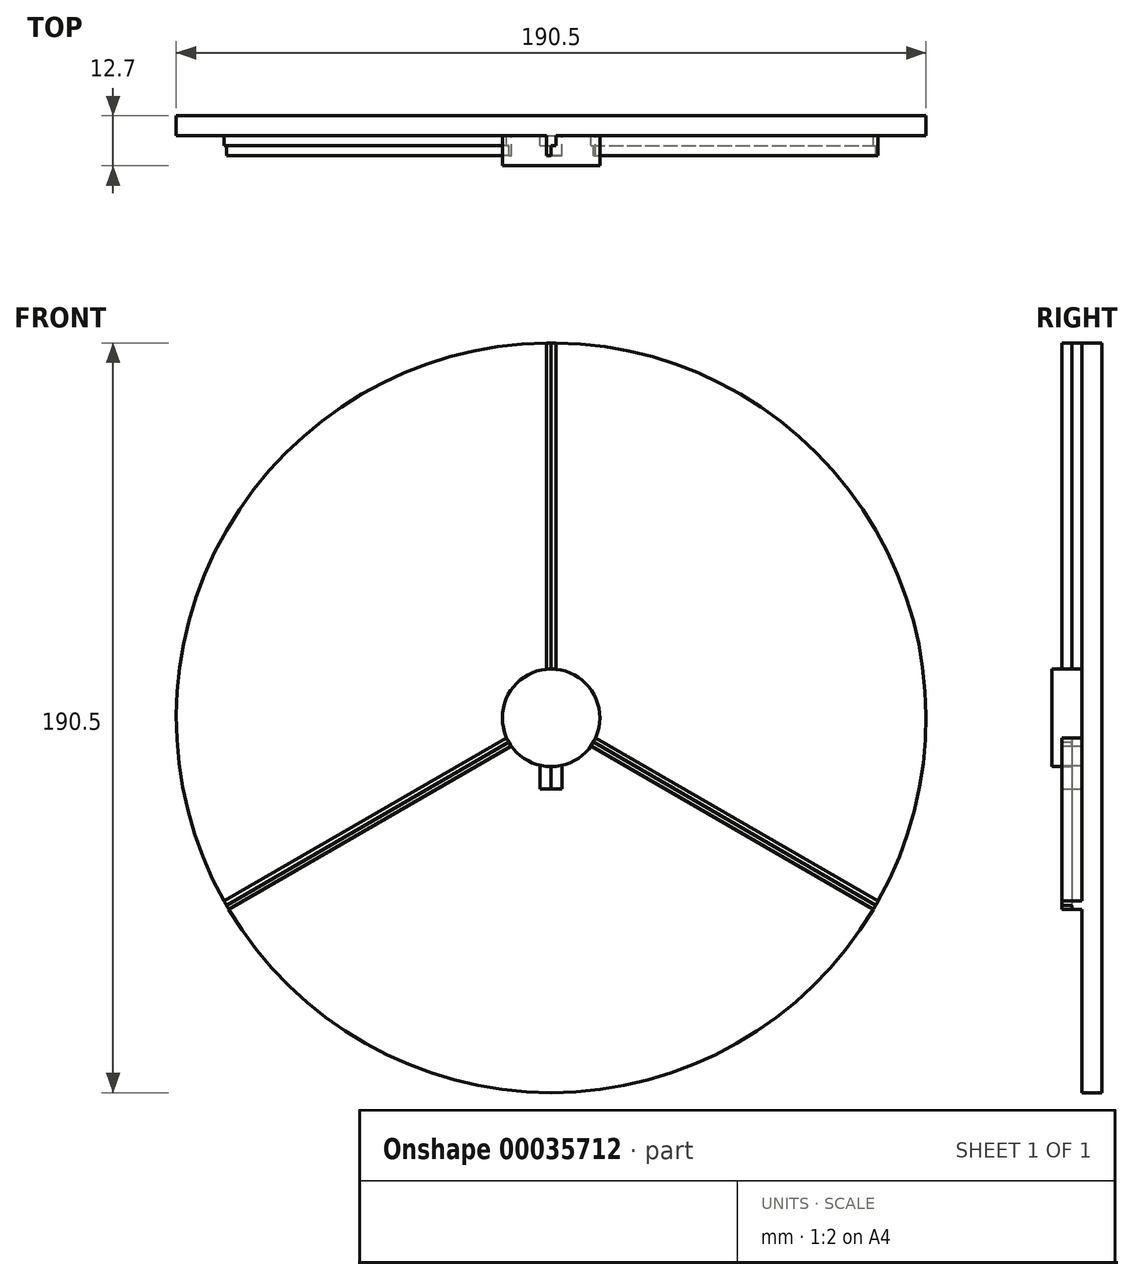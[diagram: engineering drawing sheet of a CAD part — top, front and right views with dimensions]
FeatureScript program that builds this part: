
annotation { "Feature Type Name" : "Feature", "Feature Type Description" : "" }
export const myFeature = defineFeature(function(context is Context, id is Id, definition is map)
    precondition{}
    {
        {
            var Q0;
            Q0=qCreatedBy(makeId("Front.planeOp"),FACE);
            var sketch = newSketch(context, id + "F0", { "sketchPlane" : qUnion([Q0])});
            skCircle(sketch, "E0", {"center": v(0, 0) * mm, "radius": 95.25 * mm});
            skCircle(sketch, "E1", {"center": v(0, 0) * mm, "radius": 12.4 * mm});
            skLineSegment(sketch, "E2", {"start": v(0, 0) * mm, "end": v(0, 95.25) * mm});
            skLineSegment(sketch, "E3", {"start": v(0, 0) * mm, "end": v(82.49, -47.62) * mm});
            skLineSegment(sketch, "E4", {"start": v(0, 0) * mm, "end": v(-1.2, 0) * mm, "construction": true});
            skLineSegment(sketch, "E5", {"start": v(-1.2, 0) * mm, "end": v(-1.2, 95.24) * mm});
            skCircle(sketch, "E6", {"center": v(0, 0) * mm, "radius": 1.2 * mm, "construction": true});
            skLineSegment(sketch, "E7.MirrorCS", {"start": v(0, 0) * mm, "end": v(1.2, 0) * mm, "construction": true});
            skLineSegment(sketch, "E8.MirrorCS", {"start": v(1.2, 0) * mm, "end": v(1.2, 95.24) * mm});
            skLineSegment(sketch, "E9", {"start": v(0, 0) * mm, "end": v(0.6, 1.03) * mm, "construction": true});
            skLineSegment(sketch, "E10", {"start": v(0.6, 1.03) * mm, "end": v(83.08, -46.6) * mm});
            skLineSegment(sketch, "E11.MirrorCS", {"start": v(-0.6, -1.03) * mm, "end": v(81.89, -48.65) * mm});
            skLineSegment(sketch, "E12.MirrorCS", {"start": v(0, 0) * mm, "end": v(-0.6, -1.03) * mm, "construction": true});
            skLineSegment(sketch, "E13.MirrorCS", {"start": v(0.6, -1.03) * mm, "end": v(-81.89, -48.65) * mm});
            skLineSegment(sketch, "E14.MirrorCS", {"start": v(0, 0) * mm, "end": v(-82.49, -47.62) * mm});
            skLineSegment(sketch, "E15.MirrorCS", {"start": v(-0.6, 1.03) * mm, "end": v(-83.08, -46.6) * mm});
            skLineSegment(sketch, "E16.MirrorCS", {"start": v(0, 0) * mm, "end": v(0.6, -1.03) * mm, "construction": true});
            skLineSegment(sketch, "E17.MirrorCS", {"start": v(0, 0) * mm, "end": v(-0.6, 1.03) * mm, "construction": true});
            skLineSegment(sketch, "E18", {"start": v(0, 0) * mm, "end": v(0, -95.25) * mm});
            skCircle(sketch, "E19", {"center": v(0, -14.57) * mm, "radius": 2.17 * mm});
            skCircle(sketch, "E20", {"center": v(0, -15.21) * mm, "radius": 2.82 * mm});
            skLineSegment(sketch, "E21", {"start": v(0, 0) * mm, "end": v(-2.82, 0) * mm, "construction": true});
            skLineSegment(sketch, "E22", {"start": v(-2.82, 0) * mm, "end": v(-2.82, -15.21) * mm});
            skLineSegment(sketch, "E23", {"start": v(0, 0) * mm, "end": v(-2.17, 0) * mm, "construction": true});
            skLineSegment(sketch, "E24", {"start": v(-2.17, 0) * mm, "end": v(-2.17, -14.57) * mm});
            skLineSegment(sketch, "E25", {"start": v(-2.82, -15.21) * mm, "end": v(-2.82, -18.03) * mm});
            skLineSegment(sketch, "E26", {"start": v(-2.82, -18.03) * mm, "end": v(0, -18.03) * mm});
            skLineSegment(sketch, "E27", {"start": v(-2.17, -14.57) * mm, "end": v(-2.17, -16.74) * mm});
            skLineSegment(sketch, "E28", {"start": v(-2.17, -16.74) * mm, "end": v(0, -16.74) * mm});
            skLineSegment(sketch, "E29.MirrorCS", {"start": v(2.17, -16.74) * mm, "end": v(0, -16.74) * mm});
            skLineSegment(sketch, "E30.MirrorCS", {"start": v(2.17, -14.57) * mm, "end": v(2.17, -16.74) * mm});
            skLineSegment(sketch, "E31.MirrorCS", {"start": v(2.82, -15.21) * mm, "end": v(2.82, -18.03) * mm});
            skLineSegment(sketch, "E32.MirrorCS", {"start": v(2.82, -18.03) * mm, "end": v(0, -18.03) * mm});
            skLineSegment(sketch, "E33.MirrorCS", {"start": v(2.82, 0) * mm, "end": v(2.82, -15.21) * mm});
            skLineSegment(sketch, "E34.MirrorCS", {"start": v(2.17, 0) * mm, "end": v(2.17, -14.57) * mm});
            skLineSegment(sketch, "E35.MirrorCS", {"start": v(0, 0) * mm, "end": v(2.17, 0) * mm, "construction": true});
            skLineSegment(sketch, "E36.MirrorCS", {"start": v(0, 0) * mm, "end": v(2.82, 0) * mm, "construction": true});
            skLineSegment(sketch, "E37", {"start": v(0, 0) * mm, "end": v(-82.49, 47.62) * mm});
            skLineSegment(sketch, "E38", {"start": v(0, 0) * mm, "end": v(82.49, 47.62) * mm});
            skLineSegment(sketch, "E39", {"start": v(0, 95.25) * mm, "end": v(0, 97.8) * mm});
            skLineSegment(sketch, "E40", {"start": v(0, 97.8) * mm, "end": v(-97.8, 97.8) * mm});
            skLineSegment(sketch, "E41", {"start": v(-97.8, 97.8) * mm, "end": v(-97.8, -97.8) * mm});
            skLineSegment(sketch, "E42", {"start": v(-97.8, -97.8) * mm, "end": v(0, -97.8) * mm});
            skLineSegment(sketch, "E43", {"start": v(0, -97.8) * mm, "end": v(0, -95.25) * mm});
            skLineSegment(sketch, "E44.MirrorCS", {"start": v(0, 97.8) * mm, "end": v(97.8, 97.8) * mm});
            skLineSegment(sketch, "E45.MirrorCS", {"start": v(97.8, 97.8) * mm, "end": v(97.8, -97.8) * mm});
            skLineSegment(sketch, "E46.MirrorCS", {"start": v(97.8, -97.8) * mm, "end": v(0, -97.8) * mm});
            skSolve(sketch);
        }
        {
            var Q0;
            {var subQ5=sQuery(id+"F0.wireOp",EDGE,"E39");Q0=makeQuery(id+"F0.imprint","IMPRINT",FACE,{"disambiguationData":[TD([[makeQuery(id+"F0.imprint","IMPRINT",EDGE,{"derivedFrom":subQ5}),-1.0]])]});}
            var Q1;
            {var subQ4=sQuery(id+"F0.wireOp",EDGE,"E39");Q1=makeQuery(id+"F0.imprint","IMPRINT",FACE,{"disambiguationData":[TD([[makeQuery(id+"F0.imprint","IMPRINT",EDGE,{"derivedFrom":subQ4}),1.0]])]});}
            var Q2;
            {var subQ3=sQuery(id+"F0.wireOp",EDGE,"E0");var subQ5=sQuery(id+"F0.wireOp",EDGE,"E5");var subQ7=makeQuery(id+"F0.imprint","INTERSECT",VERTEX,{"derivedFrom":[subQ3,subQ5]});Q2=makeQuery(id+"F0.imprint","IMPRINT",FACE,{"disambiguationData":[TD([[makeQuery(id+"F0.imprint","IMPRINT",EDGE,{"disambiguationData":[TD([[subQ7,-1.0]])],"derivedFrom":subQ3}),1.0]])]});}
            var Q3;
            {var subQ0=sQuery(id+"F0.wireOp",EDGE,"E24");var subQ3=sQuery(id+"F0.wireOp",EDGE,"E1");var subQ4=makeQuery(id+"F0.imprint","INTERSECT",VERTEX,{"derivedFrom":[subQ3,subQ0]});Q3=makeQuery(id+"F0.imprint","IMPRINT",FACE,{"disambiguationData":[TD([[makeQuery(id+"F0.imprint","IMPRINT",EDGE,{"disambiguationData":[TD([[subQ4,1.0]])],"derivedFrom":subQ0}),1.0]])]});}
            var Q4;
            {var subQ4=sQuery(id+"F0.wireOp",EDGE,"E31.MirrorCS");Q4=makeQuery(id+"F0.imprint","IMPRINT",FACE,{"disambiguationData":[TD([[makeQuery(id+"F0.imprint","IMPRINT",EDGE,{"derivedFrom":subQ4}),1.0]])]});}
            var Q5;
            {var subQ1=sQuery(id+"F0.wireOp",EDGE,"E8.MirrorCS");var subQ3=sQuery(id+"F0.wireOp",EDGE,"E1");var subQ5=makeQuery(id+"F0.imprint","INTERSECT",VERTEX,{"derivedFrom":[subQ3,subQ1]});Q5=makeQuery(id+"F0.imprint","IMPRINT",FACE,{"disambiguationData":[TD([[makeQuery(id+"F0.imprint","IMPRINT",EDGE,{"disambiguationData":[TD([[subQ5,1.0]])],"derivedFrom":subQ3}),1.0]])]});}
            var Q6;
            {var subQ1=sQuery(id+"F0.wireOp",EDGE,"E5");var subQ3=sQuery(id+"F0.wireOp",EDGE,"E1");var subQ5=makeQuery(id+"F0.imprint","INTERSECT",VERTEX,{"derivedFrom":[subQ3,subQ1]});Q6=makeQuery(id+"F0.imprint","IMPRINT",FACE,{"disambiguationData":[TD([[makeQuery(id+"F0.imprint","IMPRINT",EDGE,{"disambiguationData":[TD([[subQ5,-1.0]])],"derivedFrom":subQ3}),1.0]])]});}
            var Q7;
            {var subQ1=sQuery(id+"F0.wireOp",EDGE,"E13.MirrorCS");var subQ3=sQuery(id+"F0.wireOp",EDGE,"E1");var subQ5=makeQuery(id+"F0.imprint","INTERSECT",VERTEX,{"derivedFrom":[subQ3,subQ1]});Q7=makeQuery(id+"F0.imprint","IMPRINT",FACE,{"disambiguationData":[TD([[makeQuery(id+"F0.imprint","IMPRINT",EDGE,{"disambiguationData":[TD([[subQ5,-1.0]])],"derivedFrom":subQ3}),1.0]])]});}
            var Q8;
            {var subQ0=sQuery(id+"F0.wireOp",EDGE,"E33.MirrorCS");var subQ3=sQuery(id+"F0.wireOp",EDGE,"E1");var subQ4=makeQuery(id+"F0.imprint","INTERSECT",VERTEX,{"derivedFrom":[subQ3,subQ0]});Q8=makeQuery(id+"F0.imprint","IMPRINT",FACE,{"disambiguationData":[TD([[makeQuery(id+"F0.imprint","IMPRINT",EDGE,{"disambiguationData":[TD([[subQ4,-1.0]])],"derivedFrom":subQ3}),1.0]])]});}
            var Q9;
            {var subQ5=sQuery(id+"F0.wireOp",EDGE,"E25");Q9=makeQuery(id+"F0.imprint","IMPRINT",FACE,{"disambiguationData":[TD([[makeQuery(id+"F0.imprint","IMPRINT",EDGE,{"derivedFrom":subQ5}),-1.0]])]});}
            var Q10;
            {var subQ3=sQuery(id+"F0.wireOp",EDGE,"E0");var subQ5=sQuery(id+"F0.wireOp",EDGE,"E15.MirrorCS");var subQ7=makeQuery(id+"F0.imprint","INTERSECT",VERTEX,{"derivedFrom":[subQ3,subQ5]});Q10=makeQuery(id+"F0.imprint","IMPRINT",FACE,{"disambiguationData":[TD([[makeQuery(id+"F0.imprint","IMPRINT",EDGE,{"disambiguationData":[TD([[subQ7,1.0]])],"derivedFrom":subQ3}),1.0]])]});}
            var Q11;
            {var subQ0=sQuery(id+"F0.wireOp",EDGE,"E37");var subQ3=sQuery(id+"F0.wireOp",EDGE,"E1");var subQ4=makeQuery(id+"F0.imprint","INTERSECT",VERTEX,{"derivedFrom":[subQ3,subQ0]});Q11=makeQuery(id+"F0.imprint","IMPRINT",FACE,{"disambiguationData":[TD([[makeQuery(id+"F0.imprint","IMPRINT",EDGE,{"disambiguationData":[TD([[subQ4,-1.0]])],"derivedFrom":subQ3}),1.0]])]});}
            var Q12;
            {var subQ0=sQuery(id+"F0.wireOp",EDGE,"E10");var subQ3=sQuery(id+"F0.wireOp",EDGE,"E0");var subQ4=makeQuery(id+"F0.imprint","INTERSECT",VERTEX,{"derivedFrom":[subQ3,subQ0]});Q12=makeQuery(id+"F0.imprint","IMPRINT",FACE,{"disambiguationData":[TD([[makeQuery(id+"F0.imprint","IMPRINT",EDGE,{"disambiguationData":[TD([[subQ4,-1.0]])],"derivedFrom":subQ3}),1.0]])]});}
            var Q13;
            {var subQ3=sQuery(id+"F0.wireOp",EDGE,"E0");var subQ5=sQuery(id+"F0.wireOp",EDGE,"E8.MirrorCS");var subQ7=makeQuery(id+"F0.imprint","INTERSECT",VERTEX,{"derivedFrom":[subQ3,subQ5]});Q13=makeQuery(id+"F0.imprint","IMPRINT",FACE,{"disambiguationData":[TD([[makeQuery(id+"F0.imprint","IMPRINT",EDGE,{"disambiguationData":[TD([[subQ7,1.0]])],"derivedFrom":subQ3}),1.0]])]});}
            var Q14;
            {var subQ5=sQuery(id+"F0.wireOp",EDGE,"E1");var subQ7=sQuery(id+"F0.wireOp",EDGE,"E38");var subQ8=makeQuery(id+"F0.imprint","INTERSECT",VERTEX,{"derivedFrom":[subQ5,subQ7]});Q14=makeQuery(id+"F0.imprint","IMPRINT",FACE,{"disambiguationData":[TD([[makeQuery(id+"F0.imprint","IMPRINT",EDGE,{"disambiguationData":[TD([[subQ8,1.0]])],"derivedFrom":subQ5}),1.0]])]});}
            var Q15;
            {var subQ0=sQuery(id+"F0.wireOp",EDGE,"E34.MirrorCS");var subQ3=sQuery(id+"F0.wireOp",EDGE,"E1");var subQ4=makeQuery(id+"F0.imprint","INTERSECT",VERTEX,{"derivedFrom":[subQ3,subQ0]});Q15=makeQuery(id+"F0.imprint","IMPRINT",FACE,{"disambiguationData":[TD([[makeQuery(id+"F0.imprint","IMPRINT",EDGE,{"disambiguationData":[TD([[subQ4,1.0]])],"derivedFrom":subQ0}),-1.0]])]});}
            var Q16;
            {var subQ0=sQuery(id+"F0.wireOp",EDGE,"E24");var subQ3=sQuery(id+"F0.wireOp",EDGE,"E1");var subQ4=makeQuery(id+"F0.imprint","INTERSECT",VERTEX,{"derivedFrom":[subQ3,subQ0]});Q16=makeQuery(id+"F0.imprint","IMPRINT",FACE,{"disambiguationData":[TD([[makeQuery(id+"F0.imprint","IMPRINT",EDGE,{"disambiguationData":[TD([[subQ4,-1.0]])],"derivedFrom":subQ0}),1.0]])]});}
            var Q17;
            {var subQ3=sQuery(id+"F0.wireOp",EDGE,"E3");var subQ5=sQuery(id+"F0.wireOp",EDGE,"E1");var subQ7=makeQuery(id+"F0.imprint","INTERSECT",VERTEX,{"derivedFrom":[subQ5,subQ3]});Q17=makeQuery(id+"F0.imprint","IMPRINT",FACE,{"disambiguationData":[TD([[makeQuery(id+"F0.imprint","IMPRINT",EDGE,{"disambiguationData":[TD([[subQ7,-1.0]])],"derivedFrom":subQ5}),1.0]])]});}
            var Q18;
            {var subQ3=sQuery(id+"F0.wireOp",EDGE,"E1");var subQ5=sQuery(id+"F0.wireOp",EDGE,"E22");var subQ7=makeQuery(id+"F0.imprint","INTERSECT",VERTEX,{"derivedFrom":[subQ3,subQ5]});Q18=makeQuery(id+"F0.imprint","IMPRINT",FACE,{"disambiguationData":[TD([[makeQuery(id+"F0.imprint","IMPRINT",EDGE,{"disambiguationData":[TD([[subQ7,-1.0]])],"derivedFrom":subQ3}),1.0]])]});}
            var Q19;
            {var subQ1=sQuery(id+"F0.wireOp",EDGE,"E15.MirrorCS");var subQ5=sQuery(id+"F0.wireOp",EDGE,"E1");var subQ6=makeQuery(id+"F0.imprint","INTERSECT",VERTEX,{"derivedFrom":[subQ5,subQ1]});Q19=makeQuery(id+"F0.imprint","IMPRINT",FACE,{"disambiguationData":[TD([[makeQuery(id+"F0.imprint","IMPRINT",EDGE,{"disambiguationData":[TD([[subQ6,-1.0]])],"derivedFrom":subQ5}),1.0]])]});}
            var Q20;
            {var subQ0=sQuery(id+"F0.wireOp",EDGE,"E1");var subQ3=sQuery(id+"F0.wireOp",EDGE,"E8.MirrorCS");var subQ4=makeQuery(id+"F0.imprint","INTERSECT",VERTEX,{"derivedFrom":[subQ0,subQ3]});Q20=makeQuery(id+"F0.imprint","IMPRINT",FACE,{"disambiguationData":[TD([[makeQuery(id+"F0.imprint","IMPRINT",EDGE,{"disambiguationData":[TD([[subQ4,-1.0]])],"derivedFrom":subQ0}),1.0]])]});}
            var Q21;
            {var subQ0=sQuery(id+"F0.wireOp",EDGE,"E14.MirrorCS");var subQ3=sQuery(id+"F0.wireOp",EDGE,"E0");var subQ4=makeQuery(id+"F0.imprint","INTERSECT",VERTEX,{"derivedFrom":[subQ3,subQ0]});Q21=makeQuery(id+"F0.imprint","IMPRINT",FACE,{"disambiguationData":[TD([[makeQuery(id+"F0.imprint","IMPRINT",EDGE,{"disambiguationData":[TD([[subQ4,1.0]])],"derivedFrom":subQ3}),1.0]])]});}
            var Q22;
            {var subQ5=sQuery(id+"F0.wireOp",EDGE,"E1");var subQ7=sQuery(id+"F0.wireOp",EDGE,"E2");var subQ8=makeQuery(id+"F0.imprint","INTERSECT",VERTEX,{"derivedFrom":[subQ5,subQ7]});Q22=makeQuery(id+"F0.imprint","IMPRINT",FACE,{"disambiguationData":[TD([[makeQuery(id+"F0.imprint","IMPRINT",EDGE,{"disambiguationData":[TD([[subQ8,-1.0]])],"derivedFrom":subQ5}),1.0]])]});}
            var Q23;
            {var subQ3=sQuery(id+"F0.wireOp",EDGE,"E0");var subQ5=sQuery(id+"F0.wireOp",EDGE,"E13.MirrorCS");var subQ7=makeQuery(id+"F0.imprint","INTERSECT",VERTEX,{"derivedFrom":[subQ3,subQ5]});Q23=makeQuery(id+"F0.imprint","IMPRINT",FACE,{"disambiguationData":[TD([[makeQuery(id+"F0.imprint","IMPRINT",EDGE,{"disambiguationData":[TD([[subQ7,1.0]])],"derivedFrom":subQ3}),1.0]])]});}
            var Q24;
            {var subQ0=sQuery(id+"F0.wireOp",EDGE,"E24");var subQ3=sQuery(id+"F0.wireOp",EDGE,"E13.MirrorCS");var subQ4=makeQuery(id+"F0.imprint","INTERSECT",VERTEX,{"derivedFrom":[subQ3,subQ0]});Q24=makeQuery(id+"F0.imprint","IMPRINT",FACE,{"disambiguationData":[TD([[makeQuery(id+"F0.imprint","IMPRINT",EDGE,{"disambiguationData":[TD([[subQ4,-1.0]])],"derivedFrom":subQ3}),-1.0]])]});}
            var Q25;
            {var subQ0=sQuery(id+"F0.wireOp",EDGE,"E2");var subQ1=sQuery(id+"F0.wireOp",EDGE,"E1");var subQ2=makeQuery(id+"F0.imprint","INTERSECT",VERTEX,{"derivedFrom":[subQ1,subQ0]});Q25=makeQuery(id+"F0.imprint","IMPRINT",FACE,{"disambiguationData":[TD([[makeQuery(id+"F0.imprint","IMPRINT",EDGE,{"disambiguationData":[TD([[subQ2,-1.0]])],"derivedFrom":subQ1}),-1.0]])]});}
            var Q26;
            {var subQ1=sQuery(id+"F0.wireOp",EDGE,"E11.MirrorCS");var subQ5=sQuery(id+"F0.wireOp",EDGE,"E1");var subQ6=makeQuery(id+"F0.imprint","INTERSECT",VERTEX,{"derivedFrom":[subQ5,subQ1]});Q26=makeQuery(id+"F0.imprint","IMPRINT",FACE,{"disambiguationData":[TD([[makeQuery(id+"F0.imprint","IMPRINT",EDGE,{"disambiguationData":[TD([[subQ6,-1.0]])],"derivedFrom":subQ5}),1.0]])]});}
            var Q27;
            {var subQ1=sQuery(id+"F0.wireOp",EDGE,"E14.MirrorCS");var subQ5=sQuery(id+"F0.wireOp",EDGE,"E1");var subQ6=makeQuery(id+"F0.imprint","INTERSECT",VERTEX,{"derivedFrom":[subQ5,subQ1]});Q27=makeQuery(id+"F0.imprint","IMPRINT",FACE,{"disambiguationData":[TD([[makeQuery(id+"F0.imprint","IMPRINT",EDGE,{"disambiguationData":[TD([[subQ6,-1.0]])],"derivedFrom":subQ5}),1.0]])]});}
            var Q28;
            {var subQ3=sQuery(id+"F0.wireOp",EDGE,"E0");var subQ5=sQuery(id+"F0.wireOp",EDGE,"E3");var subQ7=makeQuery(id+"F0.imprint","INTERSECT",VERTEX,{"derivedFrom":[subQ3,subQ5]});Q28=makeQuery(id+"F0.imprint","IMPRINT",FACE,{"disambiguationData":[TD([[makeQuery(id+"F0.imprint","IMPRINT",EDGE,{"disambiguationData":[TD([[subQ7,-1.0]])],"derivedFrom":subQ3}),1.0]])]});}
            var Q29;
            {var subQ3=sQuery(id+"F0.wireOp",EDGE,"E0");var subQ5=sQuery(id+"F0.wireOp",EDGE,"E3");var subQ7=makeQuery(id+"F0.imprint","INTERSECT",VERTEX,{"derivedFrom":[subQ3,subQ5]});Q29=makeQuery(id+"F0.imprint","IMPRINT",FACE,{"disambiguationData":[TD([[makeQuery(id+"F0.imprint","IMPRINT",EDGE,{"disambiguationData":[TD([[subQ7,1.0]])],"derivedFrom":subQ3}),1.0]])]});}
            var Q30;
            {var subQ1=sQuery(id+"F0.wireOp",EDGE,"E1");var subQ5=sQuery(id+"F0.wireOp",EDGE,"E8.MirrorCS");var subQ6=makeQuery(id+"F0.imprint","INTERSECT",VERTEX,{"derivedFrom":[subQ1,subQ5]});Q30=makeQuery(id+"F0.imprint","IMPRINT",FACE,{"disambiguationData":[TD([[makeQuery(id+"F0.imprint","IMPRINT",EDGE,{"disambiguationData":[TD([[subQ6,-1.0]])],"derivedFrom":subQ1}),-1.0]])]});}
            var Q31;
            {var subQ3=sQuery(id+"F0.wireOp",EDGE,"E3");var subQ5=sQuery(id+"F0.wireOp",EDGE,"E6");var subQ6=makeQuery(id+"F0.imprint","INTERSECT",VERTEX,{"derivedFrom":[subQ3,subQ5]});Q31=makeQuery(id+"F0.imprint","IMPRINT",FACE,{"disambiguationData":[TD([[makeQuery(id+"F0.imprint","IMPRINT",EDGE,{"disambiguationData":[TD([[subQ6,-1.0]])],"derivedFrom":subQ3}),-1.0]])]});}
            var Q32;
            {var subQ0=sQuery(id+"F0.wireOp",EDGE,"E34.MirrorCS");var subQ3=sQuery(id+"F0.wireOp",EDGE,"E3");var subQ4=makeQuery(id+"F0.imprint","INTERSECT",VERTEX,{"derivedFrom":[subQ3,subQ0]});Q32=makeQuery(id+"F0.imprint","IMPRINT",FACE,{"disambiguationData":[TD([[makeQuery(id+"F0.imprint","IMPRINT",EDGE,{"disambiguationData":[TD([[subQ4,-1.0]])],"derivedFrom":subQ3}),-1.0]])]});}
            var Q33;
            {var subQ0=sQuery(id+"F0.wireOp",EDGE,"E19");var subQ1=makeQuery(id+"F0.imprint","INTERSECT",VERTEX,{"derivedFrom":[subQ0,sQuery(id+"F0.wireOp",EDGE,"E30.MirrorCS"),sQuery(id+"F0.wireOp",EDGE,"E34.MirrorCS")]});Q33=makeQuery(id+"F0.imprint","IMPRINT",FACE,{"disambiguationData":[TD([[makeQuery(id+"F0.imprint","IMPRINT",EDGE,{"disambiguationData":[TD([[subQ1,-1.0]])],"derivedFrom":subQ0}),1.0]])]});}
            var Q34;
            {var subQ0=sQuery(id+"F0.wireOp",EDGE,"E6");var subQ1=sQuery(id+"F0.wireOp",EDGE,"E14.MirrorCS");var subQ2=makeQuery(id+"F0.imprint","INTERSECT",VERTEX,{"derivedFrom":[subQ0,subQ1]});Q34=makeQuery(id+"F0.imprint","IMPRINT",FACE,{"disambiguationData":[TD([[makeQuery(id+"F0.imprint","IMPRINT",EDGE,{"disambiguationData":[TD([[subQ2,-1.0]])],"derivedFrom":subQ1}),1.0]])]});}
            var Q35;
            {var subQ3=sQuery(id+"F0.wireOp",EDGE,"E1");var subQ5=sQuery(id+"F0.wireOp",EDGE,"E34.MirrorCS");var subQ7=makeQuery(id+"F0.imprint","INTERSECT",VERTEX,{"derivedFrom":[subQ3,subQ5]});Q35=makeQuery(id+"F0.imprint","IMPRINT",FACE,{"disambiguationData":[TD([[makeQuery(id+"F0.imprint","IMPRINT",EDGE,{"disambiguationData":[TD([[subQ7,-1.0]])],"derivedFrom":subQ3}),1.0]])]});}
            var Q36;
            {var subQ3=sQuery(id+"F0.wireOp",EDGE,"E1");var subQ5=sQuery(id+"F0.wireOp",EDGE,"E22");var subQ6=makeQuery(id+"F0.imprint","INTERSECT",VERTEX,{"derivedFrom":[subQ3,subQ5]});Q36=makeQuery(id+"F0.imprint","IMPRINT",FACE,{"disambiguationData":[TD([[makeQuery(id+"F0.imprint","IMPRINT",EDGE,{"disambiguationData":[TD([[subQ6,-1.0]])],"derivedFrom":subQ3}),-1.0]])]});}
            var Q37;
            {var subQ1=sQuery(id+"F0.wireOp",EDGE,"E1");var subQ5=sQuery(id+"F0.wireOp",EDGE,"E34.MirrorCS");var subQ7=makeQuery(id+"F0.imprint","INTERSECT",VERTEX,{"derivedFrom":[subQ1,subQ5]});Q37=makeQuery(id+"F0.imprint","IMPRINT",FACE,{"disambiguationData":[TD([[makeQuery(id+"F0.imprint","IMPRINT",EDGE,{"disambiguationData":[TD([[subQ7,-1.0]])],"derivedFrom":subQ1}),-1.0]])]});}
            var Q38;
            {var subQ1=sQuery(id+"F0.wireOp",EDGE,"E27");Q38=makeQuery(id+"F0.imprint","IMPRINT",FACE,{"disambiguationData":[TD([[makeQuery(id+"F0.imprint","IMPRINT",EDGE,{"derivedFrom":subQ1}),1.0]])]});}
            var Q39;
            {var subQ0=sQuery(id+"F0.wireOp",EDGE,"E34.MirrorCS");var subQ1=sQuery(id+"F0.wireOp",EDGE,"E20");var subQ2=makeQuery(id+"F0.imprint","INTERSECT",VERTEX,{"derivedFrom":[subQ1,subQ0]});Q39=makeQuery(id+"F0.imprint","IMPRINT",FACE,{"disambiguationData":[TD([[makeQuery(id+"F0.imprint","IMPRINT",EDGE,{"disambiguationData":[TD([[subQ2,-1.0]])],"derivedFrom":subQ0}),-1.0]])]});}
            var Q40;
            {var subQ0=sQuery(id+"F0.wireOp",EDGE,"E34.MirrorCS");var subQ3=sQuery(id+"F0.wireOp",EDGE,"E1");var subQ4=makeQuery(id+"F0.imprint","INTERSECT",VERTEX,{"derivedFrom":[subQ3,subQ0]});Q40=makeQuery(id+"F0.imprint","IMPRINT",FACE,{"disambiguationData":[TD([[makeQuery(id+"F0.imprint","IMPRINT",EDGE,{"disambiguationData":[TD([[subQ4,-1.0]])],"derivedFrom":subQ0}),-1.0]])]});}
            var Q41;
            {var subQ1=sQuery(id+"F0.wireOp",EDGE,"E27");Q41=makeQuery(id+"F0.imprint","IMPRINT",FACE,{"disambiguationData":[TD([[makeQuery(id+"F0.imprint","IMPRINT",EDGE,{"derivedFrom":subQ1}),-1.0]])]});}
            var Q42;
            {var subQ0=sQuery(id+"F0.wireOp",EDGE,"E24");var subQ1=sQuery(id+"F0.wireOp",EDGE,"E20");var subQ2=makeQuery(id+"F0.imprint","INTERSECT",VERTEX,{"derivedFrom":[subQ1,subQ0]});Q42=makeQuery(id+"F0.imprint","IMPRINT",FACE,{"disambiguationData":[TD([[makeQuery(id+"F0.imprint","IMPRINT",EDGE,{"disambiguationData":[TD([[subQ2,-1.0]])],"derivedFrom":subQ0}),1.0]])]});}
            var Q43;
            {var subQ5=sQuery(id+"F0.wireOp",EDGE,"E29.MirrorCS");Q43=makeQuery(id+"F0.imprint","IMPRINT",FACE,{"disambiguationData":[TD([[makeQuery(id+"F0.imprint","IMPRINT",EDGE,{"derivedFrom":subQ5}),1.0]])]});}
            var Q44;
            {var subQ0=sQuery(id+"F0.wireOp",EDGE,"E19");var subQ3=makeQuery(id+"F0.imprint","INTERSECT",VERTEX,{"derivedFrom":[subQ0,sQuery(id+"F0.wireOp",EDGE,"E24"),sQuery(id+"F0.wireOp",EDGE,"E27")]});Q44=makeQuery(id+"F0.imprint","IMPRINT",FACE,{"disambiguationData":[TD([[makeQuery(id+"F0.imprint","IMPRINT",EDGE,{"disambiguationData":[TD([[subQ3,1.0]])],"derivedFrom":subQ0}),1.0]])]});}
            var Q45;
            {var subQ1=sQuery(id+"F0.wireOp",EDGE,"E29.MirrorCS");Q45=makeQuery(id+"F0.imprint","IMPRINT",FACE,{"disambiguationData":[TD([[makeQuery(id+"F0.imprint","IMPRINT",EDGE,{"derivedFrom":subQ1}),-1.0]])]});}
            var Q46;
            {var subQ1=sQuery(id+"F0.wireOp",EDGE,"E25");Q46=makeQuery(id+"F0.imprint","IMPRINT",FACE,{"disambiguationData":[TD([[makeQuery(id+"F0.imprint","IMPRINT",EDGE,{"derivedFrom":subQ1}),1.0]])]});}
            var Q47;
            {var subQ1=sQuery(id+"F0.wireOp",EDGE,"E31.MirrorCS");Q47=makeQuery(id+"F0.imprint","IMPRINT",FACE,{"disambiguationData":[TD([[makeQuery(id+"F0.imprint","IMPRINT",EDGE,{"derivedFrom":subQ1}),-1.0]])]});}
            var Q48;
            {var subQ1=sQuery(id+"F0.wireOp",EDGE,"E15.MirrorCS");var subQ3=sQuery(id+"F0.wireOp",EDGE,"E21");var subQ5=makeQuery(id+"F0.imprint","INTERSECT",VERTEX,{"derivedFrom":[subQ1,subQ3]});Q48=makeQuery(id+"F0.imprint","IMPRINT",FACE,{"disambiguationData":[TD([[makeQuery(id+"F0.imprint","IMPRINT",EDGE,{"disambiguationData":[TD([[subQ5,-1.0]])],"derivedFrom":subQ1}),-1.0]])]});}
            var Q49;
            {var subQ0=sQuery(id+"F0.wireOp",EDGE,"E3");var subQ3=sQuery(id+"F0.wireOp",EDGE,"E34.MirrorCS");var subQ4=makeQuery(id+"F0.imprint","INTERSECT",VERTEX,{"derivedFrom":[subQ0,subQ3]});Q49=makeQuery(id+"F0.imprint","IMPRINT",FACE,{"disambiguationData":[TD([[makeQuery(id+"F0.imprint","IMPRINT",EDGE,{"disambiguationData":[TD([[subQ4,-1.0]])],"derivedFrom":subQ0}),1.0]])]});}
            var Q50;
            {var subQ0=sQuery(id+"F0.wireOp",EDGE,"E24");var subQ1=sQuery(id+"F0.wireOp",EDGE,"E14.MirrorCS");var subQ2=makeQuery(id+"F0.imprint","INTERSECT",VERTEX,{"derivedFrom":[subQ1,subQ0]});Q50=makeQuery(id+"F0.imprint","IMPRINT",FACE,{"disambiguationData":[TD([[makeQuery(id+"F0.imprint","IMPRINT",EDGE,{"disambiguationData":[TD([[subQ2,-1.0]])],"derivedFrom":subQ1}),-1.0]])]});}
            var Q51;
            {var subQ1=sQuery(id+"F0.wireOp",EDGE,"E14.MirrorCS");var subQ5=sQuery(id+"F0.wireOp",EDGE,"E6");var subQ7=makeQuery(id+"F0.imprint","INTERSECT",VERTEX,{"derivedFrom":[subQ5,subQ1]});Q51=makeQuery(id+"F0.imprint","IMPRINT",FACE,{"disambiguationData":[TD([[makeQuery(id+"F0.imprint","IMPRINT",EDGE,{"disambiguationData":[TD([[subQ7,-1.0]])],"derivedFrom":subQ1}),-1.0]])]});}
            var Q52;
            {var subQ1=sQuery(id+"F0.wireOp",EDGE,"E3");var subQ5=sQuery(id+"F0.wireOp",EDGE,"E6");var subQ7=makeQuery(id+"F0.imprint","INTERSECT",VERTEX,{"derivedFrom":[subQ1,subQ5]});Q52=makeQuery(id+"F0.imprint","IMPRINT",FACE,{"disambiguationData":[TD([[makeQuery(id+"F0.imprint","IMPRINT",EDGE,{"disambiguationData":[TD([[subQ7,-1.0]])],"derivedFrom":subQ1}),1.0]])]});}
            var Q53;
            {var subQ0=sQuery(id+"F0.wireOp",EDGE,"E37");var subQ3=sQuery(id+"F0.wireOp",EDGE,"E6");var subQ4=makeQuery(id+"F0.imprint","INTERSECT",VERTEX,{"derivedFrom":[subQ3,subQ0]});Q53=makeQuery(id+"F0.imprint","IMPRINT",FACE,{"disambiguationData":[TD([[makeQuery(id+"F0.imprint","IMPRINT",EDGE,{"disambiguationData":[TD([[subQ4,1.0]])],"derivedFrom":subQ3}),-1.0]])]});}
            var Q54;
            {var subQ0=sQuery(id+"F0.wireOp",EDGE,"E16.MirrorCS");Q54=makeQuery(id+"F0.imprint","IMPRINT",FACE,{"disambiguationData":[TD([[makeQuery(id+"F0.imprint","IMPRINT",EDGE,{"derivedFrom":subQ0}),-1.0]])]});}
            var Q55;
            {var subQ3=sQuery(id+"F0.wireOp",EDGE,"E36.MirrorCS");var subQ5=makeQuery(id+"F0.imprint","INTERSECT",VERTEX,{"derivedFrom":[sQuery(id+"F0.wireOp",EDGE,"E34.MirrorCS"),subQ3]});Q55=makeQuery(id+"F0.imprint","IMPRINT",FACE,{"disambiguationData":[TD([[makeQuery(id+"F0.imprint","IMPRINT",EDGE,{"disambiguationData":[TD([[subQ5,-1.0]])],"derivedFrom":subQ3}),1.0]])]});}
            var Q56;
            {var subQ0=sQuery(id+"F0.wireOp",EDGE,"E18");var subQ3=sQuery(id+"F0.wireOp",EDGE,"E6");var subQ4=makeQuery(id+"F0.imprint","INTERSECT",VERTEX,{"derivedFrom":[subQ3,subQ0]});Q56=makeQuery(id+"F0.imprint","IMPRINT",FACE,{"disambiguationData":[TD([[makeQuery(id+"F0.imprint","IMPRINT",EDGE,{"disambiguationData":[TD([[subQ4,1.0]])],"derivedFrom":subQ3}),-1.0]])]});}
            var Q57;
            {var subQ1=sQuery(id+"F0.wireOp",EDGE,"E18");var subQ3=sQuery(id+"F0.wireOp",EDGE,"E6");var subQ5=makeQuery(id+"F0.imprint","INTERSECT",VERTEX,{"derivedFrom":[subQ3,subQ1]});Q57=makeQuery(id+"F0.imprint","IMPRINT",FACE,{"disambiguationData":[TD([[makeQuery(id+"F0.imprint","IMPRINT",EDGE,{"disambiguationData":[TD([[subQ5,-1.0]])],"derivedFrom":subQ3}),-1.0]])]});}
            var Q58;
            {var subQ0=sQuery(id+"F0.wireOp",EDGE,"E37");var subQ3=sQuery(id+"F0.wireOp",EDGE,"E6");var subQ4=makeQuery(id+"F0.imprint","INTERSECT",VERTEX,{"derivedFrom":[subQ3,subQ0]});Q58=makeQuery(id+"F0.imprint","IMPRINT",FACE,{"disambiguationData":[TD([[makeQuery(id+"F0.imprint","IMPRINT",EDGE,{"disambiguationData":[TD([[subQ4,-1.0]])],"derivedFrom":subQ3}),-1.0]])]});}
            var Q59;
            {var subQ1=sQuery(id+"F0.wireOp",EDGE,"E6");var subQ3=sQuery(id+"F0.wireOp",EDGE,"E3");var subQ5=makeQuery(id+"F0.imprint","INTERSECT",VERTEX,{"derivedFrom":[subQ3,subQ1]});Q59=makeQuery(id+"F0.imprint","IMPRINT",FACE,{"disambiguationData":[TD([[makeQuery(id+"F0.imprint","IMPRINT",EDGE,{"disambiguationData":[TD([[subQ5,-1.0]])],"derivedFrom":subQ1}),1.0]])]});}
            var Q60;
            {var subQ3=sQuery(id+"F0.wireOp",EDGE,"E17.MirrorCS");Q60=makeQuery(id+"F0.imprint","IMPRINT",FACE,{"disambiguationData":[TD([[makeQuery(id+"F0.imprint","IMPRINT",EDGE,{"derivedFrom":subQ3}),1.0]])]});}
            var Q61;
            {var subQ3=sQuery(id+"F0.wireOp",EDGE,"E9");Q61=makeQuery(id+"F0.imprint","IMPRINT",FACE,{"disambiguationData":[TD([[makeQuery(id+"F0.imprint","IMPRINT",EDGE,{"derivedFrom":subQ3}),-1.0]])]});}
            var Q62;
            {var subQ1=sQuery(id+"F0.wireOp",EDGE,"E38");var subQ3=sQuery(id+"F0.wireOp",EDGE,"E6");var subQ5=makeQuery(id+"F0.imprint","INTERSECT",VERTEX,{"derivedFrom":[subQ3,subQ1]});Q62=makeQuery(id+"F0.imprint","IMPRINT",FACE,{"disambiguationData":[TD([[makeQuery(id+"F0.imprint","IMPRINT",EDGE,{"disambiguationData":[TD([[subQ5,-1.0]])],"derivedFrom":subQ3}),-1.0]])]});}
            var Q63;
            {var subQ0=sQuery(id+"F0.wireOp",EDGE,"E16.MirrorCS");Q63=makeQuery(id+"F0.imprint","IMPRINT",FACE,{"disambiguationData":[TD([[makeQuery(id+"F0.imprint","IMPRINT",EDGE,{"derivedFrom":subQ0}),1.0]])]});}
            var Q64;
            {var subQ0=sQuery(id+"F0.wireOp",EDGE,"E17.MirrorCS");Q64=makeQuery(id+"F0.imprint","IMPRINT",FACE,{"disambiguationData":[TD([[makeQuery(id+"F0.imprint","IMPRINT",EDGE,{"derivedFrom":subQ0}),-1.0]])]});}
            var Q65;
            {var subQ0=sQuery(id+"F0.wireOp",EDGE,"E21");var subQ1=sQuery(id+"F0.wireOp",EDGE,"E15.MirrorCS");var subQ2=makeQuery(id+"F0.imprint","INTERSECT",VERTEX,{"derivedFrom":[subQ1,subQ0]});Q65=makeQuery(id+"F0.imprint","IMPRINT",FACE,{"disambiguationData":[TD([[makeQuery(id+"F0.imprint","IMPRINT",EDGE,{"disambiguationData":[TD([[subQ2,1.0]])],"derivedFrom":subQ1}),1.0]])]});}
            var Q66;
            {var subQ1=sQuery(id+"F0.wireOp",EDGE,"E6");var subQ3=sQuery(id+"F0.wireOp",EDGE,"E14.MirrorCS");var subQ5=makeQuery(id+"F0.imprint","INTERSECT",VERTEX,{"derivedFrom":[subQ1,subQ3]});Q66=makeQuery(id+"F0.imprint","IMPRINT",FACE,{"disambiguationData":[TD([[makeQuery(id+"F0.imprint","IMPRINT",EDGE,{"disambiguationData":[TD([[subQ5,1.0]])],"derivedFrom":subQ1}),1.0]])]});}
            var Q67;
            {var subQ3=sQuery(id+"F0.wireOp",EDGE,"E12.MirrorCS");Q67=makeQuery(id+"F0.imprint","IMPRINT",FACE,{"disambiguationData":[TD([[makeQuery(id+"F0.imprint","IMPRINT",EDGE,{"derivedFrom":subQ3}),1.0]])]});}
            var Q68;
            {var subQ0=sQuery(id+"F0.wireOp",EDGE,"E9");Q68=makeQuery(id+"F0.imprint","IMPRINT",FACE,{"disambiguationData":[TD([[makeQuery(id+"F0.imprint","IMPRINT",EDGE,{"derivedFrom":subQ0}),1.0]])]});}
            var Q69;
            {var subQ0=sQuery(id+"F0.wireOp",EDGE,"E37");var subQ1=sQuery(id+"F0.wireOp",EDGE,"E6");var subQ2=makeQuery(id+"F0.imprint","INTERSECT",VERTEX,{"derivedFrom":[subQ1,subQ0]});Q69=makeQuery(id+"F0.imprint","IMPRINT",FACE,{"disambiguationData":[TD([[makeQuery(id+"F0.imprint","IMPRINT",EDGE,{"disambiguationData":[TD([[subQ2,-1.0]])],"derivedFrom":subQ1}),1.0]])]});}
            var Q70;
            {var subQ0=sQuery(id+"F0.wireOp",EDGE,"E38");var subQ1=sQuery(id+"F0.wireOp",EDGE,"E6");var subQ2=makeQuery(id+"F0.imprint","INTERSECT",VERTEX,{"derivedFrom":[subQ1,subQ0]});Q70=makeQuery(id+"F0.imprint","IMPRINT",FACE,{"disambiguationData":[TD([[makeQuery(id+"F0.imprint","IMPRINT",EDGE,{"disambiguationData":[TD([[subQ2,1.0]])],"derivedFrom":subQ1}),1.0]])]});}
            var Q71;
            {var subQ3=sQuery(id+"F0.wireOp",EDGE,"E12.MirrorCS");Q71=makeQuery(id+"F0.imprint","IMPRINT",FACE,{"disambiguationData":[TD([[makeQuery(id+"F0.imprint","IMPRINT",EDGE,{"derivedFrom":subQ3}),-1.0]])]});}
            var Q72;
            {var subQ0=sQuery(id+"F0.wireOp",EDGE,"E38");var subQ3=sQuery(id+"F0.wireOp",EDGE,"E6");var subQ4=makeQuery(id+"F0.imprint","INTERSECT",VERTEX,{"derivedFrom":[subQ3,subQ0]});Q72=makeQuery(id+"F0.imprint","IMPRINT",FACE,{"disambiguationData":[TD([[makeQuery(id+"F0.imprint","IMPRINT",EDGE,{"disambiguationData":[TD([[subQ4,1.0]])],"derivedFrom":subQ3}),-1.0]])]});}
            var Q73;
            {var subQ0=sQuery(id+"F0.wireOp",EDGE,"E36.MirrorCS");var subQ1=sQuery(id+"F0.wireOp",EDGE,"E10");var subQ2=makeQuery(id+"F0.imprint","INTERSECT",VERTEX,{"derivedFrom":[subQ1,subQ0]});Q73=makeQuery(id+"F0.imprint","IMPRINT",FACE,{"disambiguationData":[TD([[makeQuery(id+"F0.imprint","IMPRINT",EDGE,{"disambiguationData":[TD([[subQ2,-1.0]])],"derivedFrom":subQ1}),1.0]])]});}
            var Q74;
            {var subQ3=sQuery(id+"F0.wireOp",EDGE,"E14.MirrorCS");var subQ5=sQuery(id+"F0.wireOp",EDGE,"E24");var subQ6=makeQuery(id+"F0.imprint","INTERSECT",VERTEX,{"derivedFrom":[subQ3,subQ5]});Q74=makeQuery(id+"F0.imprint","IMPRINT",FACE,{"disambiguationData":[TD([[makeQuery(id+"F0.imprint","IMPRINT",EDGE,{"disambiguationData":[TD([[subQ6,-1.0]])],"derivedFrom":subQ5}),1.0]])]});}
            var Q75;
            {var subQ0=sQuery(id+"F0.wireOp",EDGE,"E34.MirrorCS");var subQ3=sQuery(id+"F0.wireOp",EDGE,"E3");var subQ4=makeQuery(id+"F0.imprint","INTERSECT",VERTEX,{"derivedFrom":[subQ3,subQ0]});Q75=makeQuery(id+"F0.imprint","IMPRINT",FACE,{"disambiguationData":[TD([[makeQuery(id+"F0.imprint","IMPRINT",EDGE,{"disambiguationData":[TD([[subQ4,-1.0]])],"derivedFrom":subQ0}),-1.0]])]});}
            extrude(context, id + "F1", {"entities" : qUnion([Q0, Q1, Q2, Q3, Q4, Q5, Q6, Q7, Q8, Q9, Q10, Q11, Q12, Q13, Q14, Q15, Q16, Q17, Q18, Q19, Q20, Q21, Q22, Q23, Q24, Q25, Q26, Q27, Q28, Q29, Q30, Q31, Q32, Q33, Q34, Q35, Q36, Q37, Q38, Q39, Q40, Q41, Q42, Q43, Q44, Q45, Q46, Q47, Q48, Q49, Q50, Q51, Q52, Q53, Q54, Q55, Q56, Q57, Q58, Q59, Q60, Q61, Q62, Q63, Q64, Q65, Q66, Q67, Q68, Q69, Q70, Q71, Q72, Q73, Q74, Q75]), "oppositeDirection" : true, "depth" : 2.54 * mm});
        }
        {
            var Q0;
            {var subQ0=sQuery(id+"F0.wireOp",EDGE,"E8.MirrorCS");var subQ1=sQuery(id+"F0.wireOp",EDGE,"E1");var subQ2=makeQuery(id+"F0.imprint","INTERSECT",VERTEX,{"derivedFrom":[subQ1,subQ0]});Q0=makeQuery(id+"F0.imprint","IMPRINT",FACE,{"disambiguationData":[TD([[makeQuery(id+"F0.imprint","IMPRINT",EDGE,{"disambiguationData":[TD([[subQ2,-1.0]])],"derivedFrom":subQ1}),-1.0]])]});}
            var Q1;
            {var subQ3=sQuery(id+"F0.wireOp",EDGE,"E0");var subQ5=sQuery(id+"F0.wireOp",EDGE,"E14.MirrorCS");var subQ7=makeQuery(id+"F0.imprint","INTERSECT",VERTEX,{"derivedFrom":[subQ3,subQ5]});Q1=makeQuery(id+"F0.imprint","IMPRINT",FACE,{"disambiguationData":[TD([[makeQuery(id+"F0.imprint","IMPRINT",EDGE,{"disambiguationData":[TD([[subQ7,1.0]])],"derivedFrom":subQ3}),1.0]])]});}
            var Q2;
            {var subQ3=sQuery(id+"F0.wireOp",EDGE,"E0");var subQ5=sQuery(id+"F0.wireOp",EDGE,"E3");var subQ7=makeQuery(id+"F0.imprint","INTERSECT",VERTEX,{"derivedFrom":[subQ3,subQ5]});Q2=makeQuery(id+"F0.imprint","IMPRINT",FACE,{"disambiguationData":[TD([[makeQuery(id+"F0.imprint","IMPRINT",EDGE,{"disambiguationData":[TD([[subQ7,1.0]])],"derivedFrom":subQ3}),1.0]])]});}
            var Q3;
            {var subQ0=sQuery(id+"F0.wireOp",EDGE,"E19");var subQ3=makeQuery(id+"F0.imprint","INTERSECT",VERTEX,{"derivedFrom":[subQ0,sQuery(id+"F0.wireOp",EDGE,"E24"),sQuery(id+"F0.wireOp",EDGE,"E27")]});Q3=makeQuery(id+"F0.imprint","IMPRINT",FACE,{"disambiguationData":[TD([[makeQuery(id+"F0.imprint","IMPRINT",EDGE,{"disambiguationData":[TD([[subQ3,1.0]])],"derivedFrom":subQ0}),1.0]])]});}
            var Q4;
            {var subQ0=sQuery(id+"F0.wireOp",EDGE,"E20");var subQ3=sQuery(id+"F0.wireOp",EDGE,"E24");var subQ4=makeQuery(id+"F0.imprint","INTERSECT",VERTEX,{"derivedFrom":[subQ0,subQ3]});Q4=makeQuery(id+"F0.imprint","IMPRINT",FACE,{"disambiguationData":[TD([[makeQuery(id+"F0.imprint","IMPRINT",EDGE,{"disambiguationData":[TD([[subQ4,-1.0]])],"derivedFrom":subQ3}),1.0]])]});}
            var Q5;
            {var subQ0=sQuery(id+"F0.wireOp",EDGE,"E24");var subQ3=sQuery(id+"F0.wireOp",EDGE,"E1");var subQ4=makeQuery(id+"F0.imprint","INTERSECT",VERTEX,{"derivedFrom":[subQ3,subQ0]});Q5=makeQuery(id+"F0.imprint","IMPRINT",FACE,{"disambiguationData":[TD([[makeQuery(id+"F0.imprint","IMPRINT",EDGE,{"disambiguationData":[TD([[subQ4,-1.0]])],"derivedFrom":subQ0}),1.0]])]});}
            var Q6;
            {var subQ3=sQuery(id+"F0.wireOp",EDGE,"E1");var subQ5=sQuery(id+"F0.wireOp",EDGE,"E22");var subQ6=makeQuery(id+"F0.imprint","INTERSECT",VERTEX,{"derivedFrom":[subQ3,subQ5]});Q6=makeQuery(id+"F0.imprint","IMPRINT",FACE,{"disambiguationData":[TD([[makeQuery(id+"F0.imprint","IMPRINT",EDGE,{"disambiguationData":[TD([[subQ6,-1.0]])],"derivedFrom":subQ3}),-1.0]])]});}
            var Q7;
            {var subQ1=sQuery(id+"F0.wireOp",EDGE,"E27");Q7=makeQuery(id+"F0.imprint","IMPRINT",FACE,{"disambiguationData":[TD([[makeQuery(id+"F0.imprint","IMPRINT",EDGE,{"derivedFrom":subQ1}),-1.0]])]});}
            var Q8;
            {var subQ1=sQuery(id+"F0.wireOp",EDGE,"E27");Q8=makeQuery(id+"F0.imprint","IMPRINT",FACE,{"disambiguationData":[TD([[makeQuery(id+"F0.imprint","IMPRINT",EDGE,{"derivedFrom":subQ1}),1.0]])]});}
            var Q9;
            {var subQ1=sQuery(id+"F0.wireOp",EDGE,"E25");Q9=makeQuery(id+"F0.imprint","IMPRINT",FACE,{"disambiguationData":[TD([[makeQuery(id+"F0.imprint","IMPRINT",EDGE,{"derivedFrom":subQ1}),1.0]])]});}
            extrude(context, id + "F2", {"entities" : qUnion([Q0, Q1, Q2, Q3, Q4, Q5, Q6, Q7, Q8, Q9]), "operationType" : NewBodyOperationType.ADD, "depth" : 5.08 * mm});
        }
        {
            var Q0;
            {var subQ1=sQuery(id+"F0.wireOp",EDGE,"E25");Q0=makeQuery(id+"F0.imprint","IMPRINT",FACE,{"disambiguationData":[TD([[makeQuery(id+"F0.imprint","IMPRINT",EDGE,{"derivedFrom":subQ1}),-1.0]])]});}
            var Q1;
            {var subQ5=sQuery(id+"F0.wireOp",EDGE,"E31.MirrorCS");Q1=makeQuery(id+"F0.imprint","IMPRINT",FACE,{"disambiguationData":[TD([[makeQuery(id+"F0.imprint","IMPRINT",EDGE,{"derivedFrom":subQ5}),1.0]])]});}
            var Q2;
            {var subQ3=sQuery(id+"F0.wireOp",EDGE,"E0");var subQ5=sQuery(id+"F0.wireOp",EDGE,"E10");var subQ7=makeQuery(id+"F0.imprint","INTERSECT",VERTEX,{"derivedFrom":[subQ3,subQ5]});Q2=makeQuery(id+"F0.imprint","IMPRINT",FACE,{"disambiguationData":[TD([[makeQuery(id+"F0.imprint","IMPRINT",EDGE,{"disambiguationData":[TD([[subQ7,-1.0]])],"derivedFrom":subQ3}),1.0]])]});}
            var Q3;
            {var subQ0=sQuery(id+"F0.wireOp",EDGE,"E8.MirrorCS");var subQ3=sQuery(id+"F0.wireOp",EDGE,"E0");var subQ4=makeQuery(id+"F0.imprint","INTERSECT",VERTEX,{"derivedFrom":[subQ3,subQ0]});Q3=makeQuery(id+"F0.imprint","IMPRINT",FACE,{"disambiguationData":[TD([[makeQuery(id+"F0.imprint","IMPRINT",EDGE,{"disambiguationData":[TD([[subQ4,1.0]])],"derivedFrom":subQ3}),1.0]])]});}
            var Q4;
            {var subQ3=sQuery(id+"F0.wireOp",EDGE,"E0");var subQ5=sQuery(id+"F0.wireOp",EDGE,"E5");var subQ7=makeQuery(id+"F0.imprint","INTERSECT",VERTEX,{"derivedFrom":[subQ3,subQ5]});Q4=makeQuery(id+"F0.imprint","IMPRINT",FACE,{"disambiguationData":[TD([[makeQuery(id+"F0.imprint","IMPRINT",EDGE,{"disambiguationData":[TD([[subQ7,-1.0]])],"derivedFrom":subQ3}),1.0]])]});}
            var Q5;
            {var subQ0=sQuery(id+"F0.wireOp",EDGE,"E15.MirrorCS");var subQ3=sQuery(id+"F0.wireOp",EDGE,"E0");var subQ4=makeQuery(id+"F0.imprint","INTERSECT",VERTEX,{"derivedFrom":[subQ3,subQ0]});Q5=makeQuery(id+"F0.imprint","IMPRINT",FACE,{"disambiguationData":[TD([[makeQuery(id+"F0.imprint","IMPRINT",EDGE,{"disambiguationData":[TD([[subQ4,1.0]])],"derivedFrom":subQ3}),1.0]])]});}
            extrude(context, id + "F3", {"entities" : qUnion([Q0, Q1, Q2, Q3, Q4, Q5]), "operationType" : NewBodyOperationType.ADD, "depth" : 2.54 * mm});
        }
        {
            var Q0;
            {var subQ0=sQuery(id+"F0.wireOp",EDGE,"E13.MirrorCS");var subQ3=sQuery(id+"F0.wireOp",EDGE,"E0");var subQ4=makeQuery(id+"F0.imprint","INTERSECT",VERTEX,{"derivedFrom":[subQ3,subQ0]});Q0=makeQuery(id+"F0.imprint","IMPRINT",FACE,{"disambiguationData":[TD([[makeQuery(id+"F0.imprint","IMPRINT",EDGE,{"disambiguationData":[TD([[subQ4,1.0]])],"derivedFrom":subQ3}),1.0]])]});}
            var Q1;
            {var subQ0=sQuery(id+"F0.wireOp",EDGE,"E3");var subQ3=sQuery(id+"F0.wireOp",EDGE,"E0");var subQ4=makeQuery(id+"F0.imprint","INTERSECT",VERTEX,{"derivedFrom":[subQ3,subQ0]});Q1=makeQuery(id+"F0.imprint","IMPRINT",FACE,{"disambiguationData":[TD([[makeQuery(id+"F0.imprint","IMPRINT",EDGE,{"disambiguationData":[TD([[subQ4,-1.0]])],"derivedFrom":subQ3}),1.0]])]});}
            var Q2;
            {var subQ1=sQuery(id+"F0.wireOp",EDGE,"E1");var subQ5=sQuery(id+"F0.wireOp",EDGE,"E2");var subQ6=makeQuery(id+"F0.imprint","INTERSECT",VERTEX,{"derivedFrom":[subQ1,subQ5]});Q2=makeQuery(id+"F0.imprint","IMPRINT",FACE,{"disambiguationData":[TD([[makeQuery(id+"F0.imprint","IMPRINT",EDGE,{"disambiguationData":[TD([[subQ6,-1.0]])],"derivedFrom":subQ1}),-1.0]])]});}
            var Q3;
            {var subQ1=sQuery(id+"F0.wireOp",EDGE,"E31.MirrorCS");Q3=makeQuery(id+"F0.imprint","IMPRINT",FACE,{"disambiguationData":[TD([[makeQuery(id+"F0.imprint","IMPRINT",EDGE,{"derivedFrom":subQ1}),-1.0]])]});}
            var Q4;
            {var subQ3=sQuery(id+"F0.wireOp",EDGE,"E29.MirrorCS");Q4=makeQuery(id+"F0.imprint","IMPRINT",FACE,{"disambiguationData":[TD([[makeQuery(id+"F0.imprint","IMPRINT",EDGE,{"derivedFrom":subQ3}),1.0]])]});}
            var Q5;
            {var subQ1=sQuery(id+"F0.wireOp",EDGE,"E29.MirrorCS");Q5=makeQuery(id+"F0.imprint","IMPRINT",FACE,{"disambiguationData":[TD([[makeQuery(id+"F0.imprint","IMPRINT",EDGE,{"derivedFrom":subQ1}),-1.0]])]});}
            var Q6;
            {var subQ0=sQuery(id+"F0.wireOp",EDGE,"E19");var subQ1=makeQuery(id+"F0.imprint","INTERSECT",VERTEX,{"derivedFrom":[subQ0,sQuery(id+"F0.wireOp",EDGE,"E30.MirrorCS"),sQuery(id+"F0.wireOp",EDGE,"E34.MirrorCS")]});Q6=makeQuery(id+"F0.imprint","IMPRINT",FACE,{"disambiguationData":[TD([[makeQuery(id+"F0.imprint","IMPRINT",EDGE,{"disambiguationData":[TD([[subQ1,-1.0]])],"derivedFrom":subQ0}),1.0]])]});}
            var Q7;
            {var subQ0=sQuery(id+"F0.wireOp",EDGE,"E20");var subQ3=sQuery(id+"F0.wireOp",EDGE,"E34.MirrorCS");var subQ4=makeQuery(id+"F0.imprint","INTERSECT",VERTEX,{"derivedFrom":[subQ0,subQ3]});Q7=makeQuery(id+"F0.imprint","IMPRINT",FACE,{"disambiguationData":[TD([[makeQuery(id+"F0.imprint","IMPRINT",EDGE,{"disambiguationData":[TD([[subQ4,-1.0]])],"derivedFrom":subQ3}),-1.0]])]});}
            var Q8;
            {var subQ0=sQuery(id+"F0.wireOp",EDGE,"E34.MirrorCS");var subQ3=sQuery(id+"F0.wireOp",EDGE,"E1");var subQ4=makeQuery(id+"F0.imprint","INTERSECT",VERTEX,{"derivedFrom":[subQ3,subQ0]});Q8=makeQuery(id+"F0.imprint","IMPRINT",FACE,{"disambiguationData":[TD([[makeQuery(id+"F0.imprint","IMPRINT",EDGE,{"disambiguationData":[TD([[subQ4,-1.0]])],"derivedFrom":subQ3}),-1.0]])]});}
            var Q9;
            {var subQ0=sQuery(id+"F0.wireOp",EDGE,"E34.MirrorCS");var subQ3=sQuery(id+"F0.wireOp",EDGE,"E1");var subQ4=makeQuery(id+"F0.imprint","INTERSECT",VERTEX,{"derivedFrom":[subQ3,subQ0]});Q9=makeQuery(id+"F0.imprint","IMPRINT",FACE,{"disambiguationData":[TD([[makeQuery(id+"F0.imprint","IMPRINT",EDGE,{"disambiguationData":[TD([[subQ4,-1.0]])],"derivedFrom":subQ0}),-1.0]])]});}
            extrude(context, id + "F4", {"entities" : qUnion([Q0, Q1, Q2, Q3, Q4, Q5, Q6, Q7, Q8, Q9]), "operationType" : NewBodyOperationType.ADD, "depth" : 7.62 * mm});
        }
        {
            var Q0;
            {var subQ1=sQuery(id+"F0.wireOp",EDGE,"E5");var subQ3=sQuery(id+"F0.wireOp",EDGE,"E1");var subQ5=makeQuery(id+"F0.imprint","INTERSECT",VERTEX,{"derivedFrom":[subQ3,subQ1]});Q0=makeQuery(id+"F0.imprint","IMPRINT",FACE,{"disambiguationData":[TD([[makeQuery(id+"F0.imprint","IMPRINT",EDGE,{"disambiguationData":[TD([[subQ5,-1.0]])],"derivedFrom":subQ3}),1.0]])]});}
            var Q1;
            {var subQ3=sQuery(id+"F0.wireOp",EDGE,"E2");var subQ5=sQuery(id+"F0.wireOp",EDGE,"E1");var subQ7=makeQuery(id+"F0.imprint","INTERSECT",VERTEX,{"derivedFrom":[subQ5,subQ3]});Q1=makeQuery(id+"F0.imprint","IMPRINT",FACE,{"disambiguationData":[TD([[makeQuery(id+"F0.imprint","IMPRINT",EDGE,{"disambiguationData":[TD([[subQ7,-1.0]])],"derivedFrom":subQ5}),1.0]])]});}
            var Q2;
            {var subQ1=sQuery(id+"F0.wireOp",EDGE,"E8.MirrorCS");var subQ5=sQuery(id+"F0.wireOp",EDGE,"E1");var subQ6=makeQuery(id+"F0.imprint","INTERSECT",VERTEX,{"derivedFrom":[subQ5,subQ1]});Q2=makeQuery(id+"F0.imprint","IMPRINT",FACE,{"disambiguationData":[TD([[makeQuery(id+"F0.imprint","IMPRINT",EDGE,{"disambiguationData":[TD([[subQ6,-1.0]])],"derivedFrom":subQ5}),1.0]])]});}
            var Q3;
            {var subQ1=sQuery(id+"F0.wireOp",EDGE,"E8.MirrorCS");var subQ3=sQuery(id+"F0.wireOp",EDGE,"E1");var subQ5=makeQuery(id+"F0.imprint","INTERSECT",VERTEX,{"derivedFrom":[subQ3,subQ1]});Q3=makeQuery(id+"F0.imprint","IMPRINT",FACE,{"disambiguationData":[TD([[makeQuery(id+"F0.imprint","IMPRINT",EDGE,{"disambiguationData":[TD([[subQ5,1.0]])],"derivedFrom":subQ3}),1.0]])]});}
            var Q4;
            {var subQ0=sQuery(id+"F0.wireOp",EDGE,"E38");var subQ3=sQuery(id+"F0.wireOp",EDGE,"E1");var subQ4=makeQuery(id+"F0.imprint","INTERSECT",VERTEX,{"derivedFrom":[subQ3,subQ0]});Q4=makeQuery(id+"F0.imprint","IMPRINT",FACE,{"disambiguationData":[TD([[makeQuery(id+"F0.imprint","IMPRINT",EDGE,{"disambiguationData":[TD([[subQ4,1.0]])],"derivedFrom":subQ3}),1.0]])]});}
            var Q5;
            {var subQ0=sQuery(id+"F0.wireOp",EDGE,"E3");var subQ1=makeQuery(id+"F0.imprint","INTERSECT",VERTEX,{"derivedFrom":[subQ0,sQuery(id+"F0.wireOp",EDGE,"E34.MirrorCS")]});Q5=makeQuery(id+"F0.imprint","IMPRINT",FACE,{"disambiguationData":[TD([[makeQuery(id+"F0.imprint","IMPRINT",EDGE,{"disambiguationData":[TD([[subQ1,-1.0]])],"derivedFrom":subQ0}),1.0]])]});}
            var Q6;
            {var subQ1=sQuery(id+"F0.wireOp",EDGE,"E3");var subQ5=sQuery(id+"F0.wireOp",EDGE,"E1");var subQ7=makeQuery(id+"F0.imprint","INTERSECT",VERTEX,{"derivedFrom":[subQ5,subQ1]});Q6=makeQuery(id+"F0.imprint","IMPRINT",FACE,{"disambiguationData":[TD([[makeQuery(id+"F0.imprint","IMPRINT",EDGE,{"disambiguationData":[TD([[subQ7,-1.0]])],"derivedFrom":subQ5}),1.0]])]});}
            var Q7;
            {var subQ1=sQuery(id+"F0.wireOp",EDGE,"E11.MirrorCS");var subQ5=sQuery(id+"F0.wireOp",EDGE,"E1");var subQ6=makeQuery(id+"F0.imprint","INTERSECT",VERTEX,{"derivedFrom":[subQ5,subQ1]});Q7=makeQuery(id+"F0.imprint","IMPRINT",FACE,{"disambiguationData":[TD([[makeQuery(id+"F0.imprint","IMPRINT",EDGE,{"disambiguationData":[TD([[subQ6,-1.0]])],"derivedFrom":subQ5}),1.0]])]});}
            var Q8;
            {var subQ0=sQuery(id+"F0.wireOp",EDGE,"E34.MirrorCS");var subQ3=sQuery(id+"F0.wireOp",EDGE,"E3");var subQ4=makeQuery(id+"F0.imprint","INTERSECT",VERTEX,{"derivedFrom":[subQ3,subQ0]});Q8=makeQuery(id+"F0.imprint","IMPRINT",FACE,{"disambiguationData":[TD([[makeQuery(id+"F0.imprint","IMPRINT",EDGE,{"disambiguationData":[TD([[subQ4,-1.0]])],"derivedFrom":subQ0}),-1.0]])]});}
            var Q9;
            {var subQ3=sQuery(id+"F0.wireOp",EDGE,"E3");var subQ5=sQuery(id+"F0.wireOp",EDGE,"E34.MirrorCS");var subQ7=makeQuery(id+"F0.imprint","INTERSECT",VERTEX,{"derivedFrom":[subQ3,subQ5]});Q9=makeQuery(id+"F0.imprint","IMPRINT",FACE,{"disambiguationData":[TD([[makeQuery(id+"F0.imprint","IMPRINT",EDGE,{"disambiguationData":[TD([[subQ7,-1.0]])],"derivedFrom":subQ3}),-1.0]])]});}
            var Q10;
            {var subQ0=sQuery(id+"F0.wireOp",EDGE,"E33.MirrorCS");var subQ3=sQuery(id+"F0.wireOp",EDGE,"E1");var subQ4=makeQuery(id+"F0.imprint","INTERSECT",VERTEX,{"derivedFrom":[subQ3,subQ0]});Q10=makeQuery(id+"F0.imprint","IMPRINT",FACE,{"disambiguationData":[TD([[makeQuery(id+"F0.imprint","IMPRINT",EDGE,{"disambiguationData":[TD([[subQ4,-1.0]])],"derivedFrom":subQ3}),1.0]])]});}
            var Q11;
            {var subQ0=sQuery(id+"F0.wireOp",EDGE,"E34.MirrorCS");var subQ3=sQuery(id+"F0.wireOp",EDGE,"E1");var subQ4=makeQuery(id+"F0.imprint","INTERSECT",VERTEX,{"derivedFrom":[subQ3,subQ0]});Q11=makeQuery(id+"F0.imprint","IMPRINT",FACE,{"disambiguationData":[TD([[makeQuery(id+"F0.imprint","IMPRINT",EDGE,{"disambiguationData":[TD([[subQ4,-1.0]])],"derivedFrom":subQ3}),1.0]])]});}
            var Q12;
            {var subQ0=sQuery(id+"F0.wireOp",EDGE,"E34.MirrorCS");var subQ3=sQuery(id+"F0.wireOp",EDGE,"E1");var subQ4=makeQuery(id+"F0.imprint","INTERSECT",VERTEX,{"derivedFrom":[subQ3,subQ0]});Q12=makeQuery(id+"F0.imprint","IMPRINT",FACE,{"disambiguationData":[TD([[makeQuery(id+"F0.imprint","IMPRINT",EDGE,{"disambiguationData":[TD([[subQ4,1.0]])],"derivedFrom":subQ0}),-1.0]])]});}
            var Q13;
            {var subQ0=sQuery(id+"F0.wireOp",EDGE,"E24");var subQ3=sQuery(id+"F0.wireOp",EDGE,"E1");var subQ4=makeQuery(id+"F0.imprint","INTERSECT",VERTEX,{"derivedFrom":[subQ3,subQ0]});Q13=makeQuery(id+"F0.imprint","IMPRINT",FACE,{"disambiguationData":[TD([[makeQuery(id+"F0.imprint","IMPRINT",EDGE,{"disambiguationData":[TD([[subQ4,1.0]])],"derivedFrom":subQ0}),1.0]])]});}
            var Q14;
            {var subQ3=sQuery(id+"F0.wireOp",EDGE,"E14.MirrorCS");var subQ7=makeQuery(id+"F0.imprint","INTERSECT",VERTEX,{"derivedFrom":[subQ3,sQuery(id+"F0.wireOp",EDGE,"E24")]});Q14=makeQuery(id+"F0.imprint","IMPRINT",FACE,{"disambiguationData":[TD([[makeQuery(id+"F0.imprint","IMPRINT",EDGE,{"disambiguationData":[TD([[subQ7,-1.0]])],"derivedFrom":subQ3}),-1.0]])]});}
            var Q15;
            {var subQ1=sQuery(id+"F0.wireOp",EDGE,"E13.MirrorCS");var subQ3=sQuery(id+"F0.wireOp",EDGE,"E1");var subQ5=makeQuery(id+"F0.imprint","INTERSECT",VERTEX,{"derivedFrom":[subQ3,subQ1]});Q15=makeQuery(id+"F0.imprint","IMPRINT",FACE,{"disambiguationData":[TD([[makeQuery(id+"F0.imprint","IMPRINT",EDGE,{"disambiguationData":[TD([[subQ5,-1.0]])],"derivedFrom":subQ3}),1.0]])]});}
            var Q16;
            {var subQ0=sQuery(id+"F0.wireOp",EDGE,"E37");var subQ3=sQuery(id+"F0.wireOp",EDGE,"E1");var subQ4=makeQuery(id+"F0.imprint","INTERSECT",VERTEX,{"derivedFrom":[subQ3,subQ0]});Q16=makeQuery(id+"F0.imprint","IMPRINT",FACE,{"disambiguationData":[TD([[makeQuery(id+"F0.imprint","IMPRINT",EDGE,{"disambiguationData":[TD([[subQ4,-1.0]])],"derivedFrom":subQ3}),1.0]])]});}
            var Q17;
            {var subQ0=sQuery(id+"F0.wireOp",EDGE,"E22");var subQ3=sQuery(id+"F0.wireOp",EDGE,"E1");var subQ4=makeQuery(id+"F0.imprint","INTERSECT",VERTEX,{"derivedFrom":[subQ3,subQ0]});Q17=makeQuery(id+"F0.imprint","IMPRINT",FACE,{"disambiguationData":[TD([[makeQuery(id+"F0.imprint","IMPRINT",EDGE,{"disambiguationData":[TD([[subQ4,-1.0]])],"derivedFrom":subQ3}),1.0]])]});}
            var Q18;
            {var subQ3=sQuery(id+"F0.wireOp",EDGE,"E14.MirrorCS");var subQ5=sQuery(id+"F0.wireOp",EDGE,"E24");var subQ6=makeQuery(id+"F0.imprint","INTERSECT",VERTEX,{"derivedFrom":[subQ3,subQ5]});Q18=makeQuery(id+"F0.imprint","IMPRINT",FACE,{"disambiguationData":[TD([[makeQuery(id+"F0.imprint","IMPRINT",EDGE,{"disambiguationData":[TD([[subQ6,-1.0]])],"derivedFrom":subQ5}),1.0]])]});}
            var Q19;
            {var subQ0=sQuery(id+"F0.wireOp",EDGE,"E24");var subQ1=sQuery(id+"F0.wireOp",EDGE,"E13.MirrorCS");var subQ2=makeQuery(id+"F0.imprint","INTERSECT",VERTEX,{"derivedFrom":[subQ1,subQ0]});Q19=makeQuery(id+"F0.imprint","IMPRINT",FACE,{"disambiguationData":[TD([[makeQuery(id+"F0.imprint","IMPRINT",EDGE,{"disambiguationData":[TD([[subQ2,-1.0]])],"derivedFrom":subQ1}),-1.0]])]});}
            var Q20;
            {var subQ1=sQuery(id+"F0.wireOp",EDGE,"E14.MirrorCS");var subQ5=sQuery(id+"F0.wireOp",EDGE,"E1");var subQ6=makeQuery(id+"F0.imprint","INTERSECT",VERTEX,{"derivedFrom":[subQ5,subQ1]});Q20=makeQuery(id+"F0.imprint","IMPRINT",FACE,{"disambiguationData":[TD([[makeQuery(id+"F0.imprint","IMPRINT",EDGE,{"disambiguationData":[TD([[subQ6,-1.0]])],"derivedFrom":subQ5}),1.0]])]});}
            var Q21;
            {var subQ3=sQuery(id+"F0.wireOp",EDGE,"E1");var subQ5=sQuery(id+"F0.wireOp",EDGE,"E15.MirrorCS");var subQ7=makeQuery(id+"F0.imprint","INTERSECT",VERTEX,{"derivedFrom":[subQ3,subQ5]});Q21=makeQuery(id+"F0.imprint","IMPRINT",FACE,{"disambiguationData":[TD([[makeQuery(id+"F0.imprint","IMPRINT",EDGE,{"disambiguationData":[TD([[subQ7,-1.0]])],"derivedFrom":subQ3}),1.0]])]});}
            extrude(context, id + "F5", {"entities" : qUnion([Q0, Q1, Q2, Q3, Q4, Q5, Q6, Q7, Q8, Q9, Q10, Q11, Q12, Q13, Q14, Q15, Q16, Q17, Q18, Q19, Q20, Q21]), "operationType" : NewBodyOperationType.ADD, "depth" : 10.16 * mm});
        }
    });
